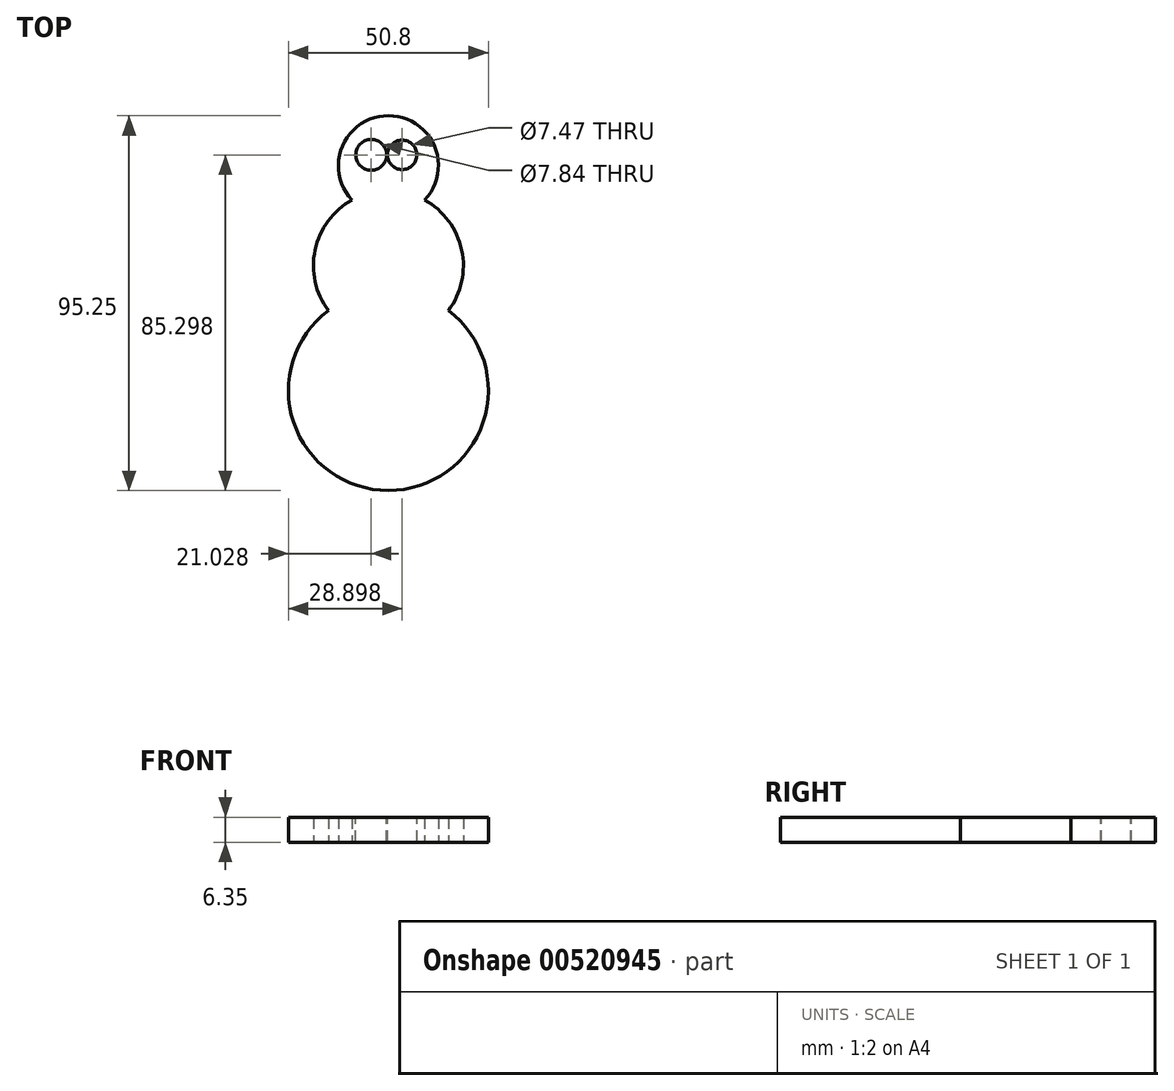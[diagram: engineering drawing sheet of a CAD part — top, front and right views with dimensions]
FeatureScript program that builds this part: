
annotation { "Feature Type Name" : "Feature", "Feature Type Description" : "" }
export const myFeature = defineFeature(function(context is Context, id is Id, definition is map)
    precondition{}
    {
        {
            var Q0;
            Q0=qCreatedBy(makeId("Top.planeOp"),FACE);
            var sketch = newSketch(context, id + "F0", { "sketchPlane" : qUnion([Q0])});
            skCircle(sketch, "E0", {"center": v(0, 0) * mm, "radius": 25.4 * mm});
            skCircle(sketch, "E1", {"center": v(0, 31.75) * mm, "radius": 19.05 * mm});
            skCircle(sketch, "E2", {"center": v(0, 57.15) * mm, "radius": 12.7 * mm});
            skSolve(sketch);
        }
        {
            var Q0;
            {var subQ0=sQuery(id+"F0.wireOp",EDGE,"E1");var subQ1=sQuery(id+"F0.wireOp",EDGE,"E0");var subQ2=makeQuery(id+"F0.imprint","INTERSECT",VERTEX,{"disambiguationData":[OD(0.0)],"derivedFrom":[subQ1,subQ0]});Q0=makeQuery(id+"F0.imprint","IMPRINT",FACE,{"disambiguationData":[TD([[makeQuery(id+"F0.imprint","IMPRINT",EDGE,{"disambiguationData":[TD([[subQ2,-1.0]])],"derivedFrom":subQ1}),1.0]])]});}
            var Q1;
            {var subQ0=sQuery(id+"F0.wireOp",EDGE,"E1");var subQ1=sQuery(id+"F0.wireOp",EDGE,"E0");var subQ2=makeQuery(id+"F0.imprint","INTERSECT",VERTEX,{"disambiguationData":[OD(0.0)],"derivedFrom":[subQ1,subQ0]});Q1=makeQuery(id+"F0.imprint","IMPRINT",FACE,{"disambiguationData":[TD([[makeQuery(id+"F0.imprint","IMPRINT",EDGE,{"disambiguationData":[TD([[subQ2,1.0]])],"derivedFrom":subQ1}),-1.0]])]});}
            var Q2;
            {var subQ0=sQuery(id+"F0.wireOp",EDGE,"E2");var subQ1=sQuery(id+"F0.wireOp",EDGE,"E1");var subQ2=makeQuery(id+"F0.imprint","INTERSECT",VERTEX,{"disambiguationData":[OD(0.0)],"derivedFrom":[subQ1,subQ0]});Q2=makeQuery(id+"F0.imprint","IMPRINT",FACE,{"disambiguationData":[TD([[makeQuery(id+"F0.imprint","IMPRINT",EDGE,{"disambiguationData":[TD([[subQ2,1.0]])],"derivedFrom":subQ1}),-1.0]])]});}
            var Q3;
            {var subQ0=sQuery(id+"F0.wireOp",EDGE,"E1");var subQ1=sQuery(id+"F0.wireOp",EDGE,"E0");var subQ2=makeQuery(id+"F0.imprint","INTERSECT",VERTEX,{"disambiguationData":[OD(0.0)],"derivedFrom":[subQ1,subQ0]});Q3=makeQuery(id+"F0.imprint","IMPRINT",FACE,{"disambiguationData":[TD([[makeQuery(id+"F0.imprint","IMPRINT",EDGE,{"disambiguationData":[TD([[subQ2,1.0]])],"derivedFrom":subQ1}),1.0]])]});}
            var Q4;
            {var subQ0=sQuery(id+"F0.wireOp",EDGE,"E2");var subQ1=sQuery(id+"F0.wireOp",EDGE,"E1");var subQ2=makeQuery(id+"F0.imprint","INTERSECT",VERTEX,{"disambiguationData":[OD(0.0)],"derivedFrom":[subQ1,subQ0]});Q4=makeQuery(id+"F0.imprint","IMPRINT",FACE,{"disambiguationData":[TD([[makeQuery(id+"F0.imprint","IMPRINT",EDGE,{"disambiguationData":[TD([[subQ2,1.0]])],"derivedFrom":subQ1}),1.0]])]});}
            extrude(context, id + "F1", {"entities" : qUnion([Q0, Q1, Q2, Q3, Q4]), "depth" : 6.35 * mm, "offsetDistance" : 25.4 * mm});
        }
        {
            var Q0;
            Q0=makeQuery(id+"F1.opExtrude","CAP_FACE",FACE,{"disambiguationData":[OSD([sQuery(id+"F0.wireOp",EDGE,"E0"),sQuery(id+"F0.wireOp",EDGE,"E1"),sQuery(id+"F0.wireOp",EDGE,"E2")])],"isStart":false});
            var sketch = newSketch(context, id + "F2", { "sketchPlane" : qUnion([Q0])});
            skCircle(sketch, "E3", {"center": v(3.5, 59.9) * mm, "radius": 3.73 * mm});
            skCircle(sketch, "E4", {"center": v(-4.37, 59.9) * mm, "radius": 3.92 * mm});
            skSolve(sketch);
        }
        {
            var Q0;
            Q0=makeQuery(id+"F2.imprint","IMPRINT",FACE,{"disambiguationData":[TD([[makeQuery(id+"F2.imprint","IMPRINT",EDGE,{"derivedFrom":sQuery(id+"F2.wireOp",EDGE,"E4")}),1.0]])]});
            var Q1;
            Q1=makeQuery(id+"F2.imprint","IMPRINT",FACE,{"disambiguationData":[TD([[makeQuery(id+"F2.imprint","IMPRINT",EDGE,{"derivedFrom":sQuery(id+"F2.wireOp",EDGE,"E3")}),1.0]])]});
            extrude(context, id + "F3", {"entities" : qUnion([Q0, Q1]), "operationType" : NewBodyOperationType.REMOVE, "oppositeDirection" : true, "depth" : 25.4 * mm, "offsetDistance" : 25.4 * mm});
        }
    });
